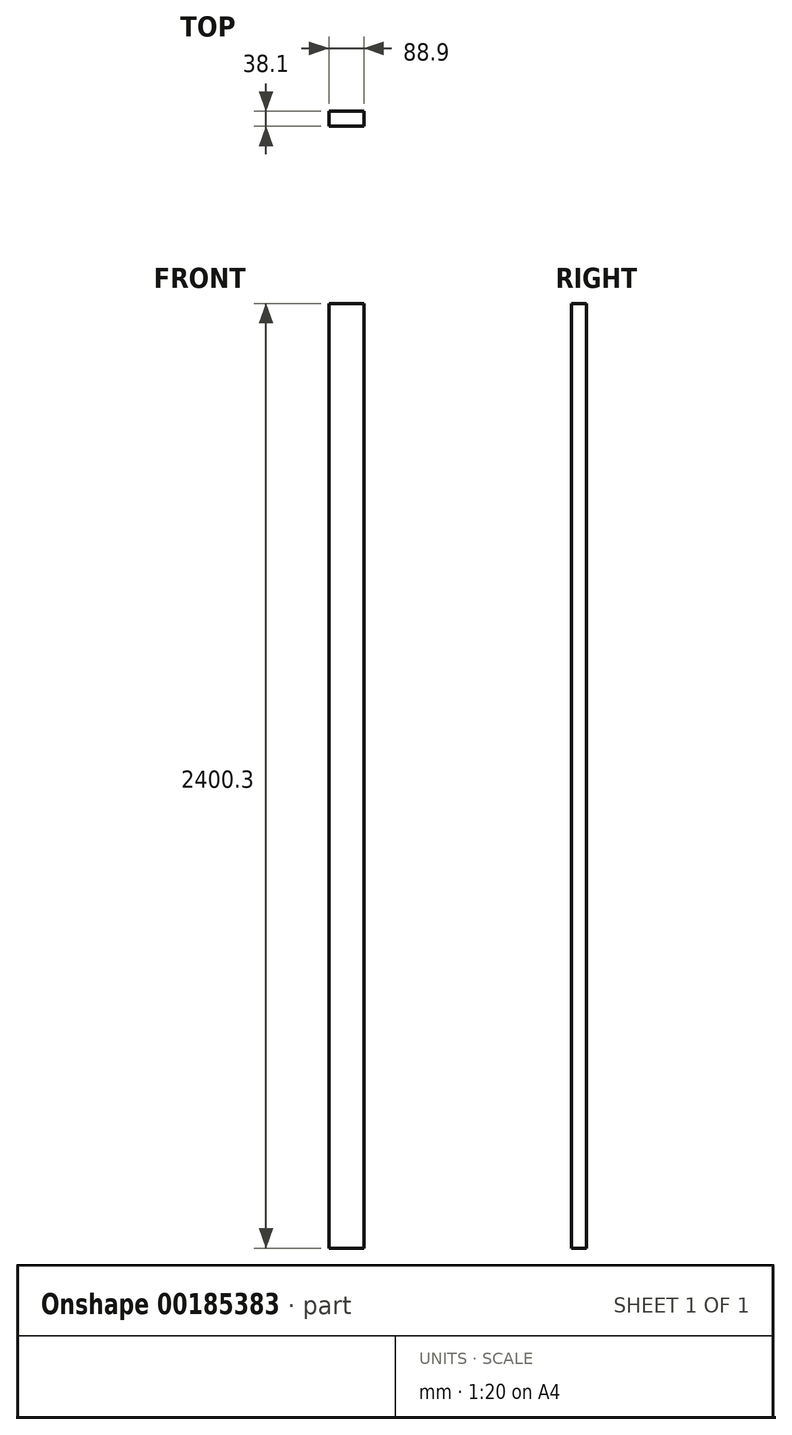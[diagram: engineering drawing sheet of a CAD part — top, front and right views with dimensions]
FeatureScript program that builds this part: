
annotation { "Feature Type Name" : "Feature", "Feature Type Description" : "" }
export const myFeature = defineFeature(function(context is Context, id is Id, definition is map)
    precondition{}
    {
        {
            var Q0;
            Q0=qCreatedBy(makeId("Top.planeOp"),FACE);
            var sketch = newSketch(context, id + "F0", { "sketchPlane" : qUnion([Q0])});
            skLineSegment(sketch, "E0.bottom", {"start": v(0, 0) * mm, "end": v(88.9, 0) * mm});
            skLineSegment(sketch, "E0.top", {"start": v(0, 38.1) * mm, "end": v(88.9, 38.1) * mm});
            skLineSegment(sketch, "E0.left", {"start": v(0, 0) * mm, "end": v(0, 38.1) * mm});
            skLineSegment(sketch, "E0.right", {"start": v(88.9, 0) * mm, "end": v(88.9, 38.1) * mm});
            skSolve(sketch);
        }
        {
            var Q0;
            Q0=makeQuery(id+"F0.imprint","IMPRINT",FACE,{"disambiguationData":[TD([[makeQuery(id+"F0.imprint","IMPRINT",EDGE,{"derivedFrom":sQuery(id+"F0.wireOp",EDGE,"E0.bottom")}),1.0]])]});
            extrude(context, id + "F1", {"entities" : qUnion([Q0]), "depth" : 2400.3 * mm});
        }
    });
